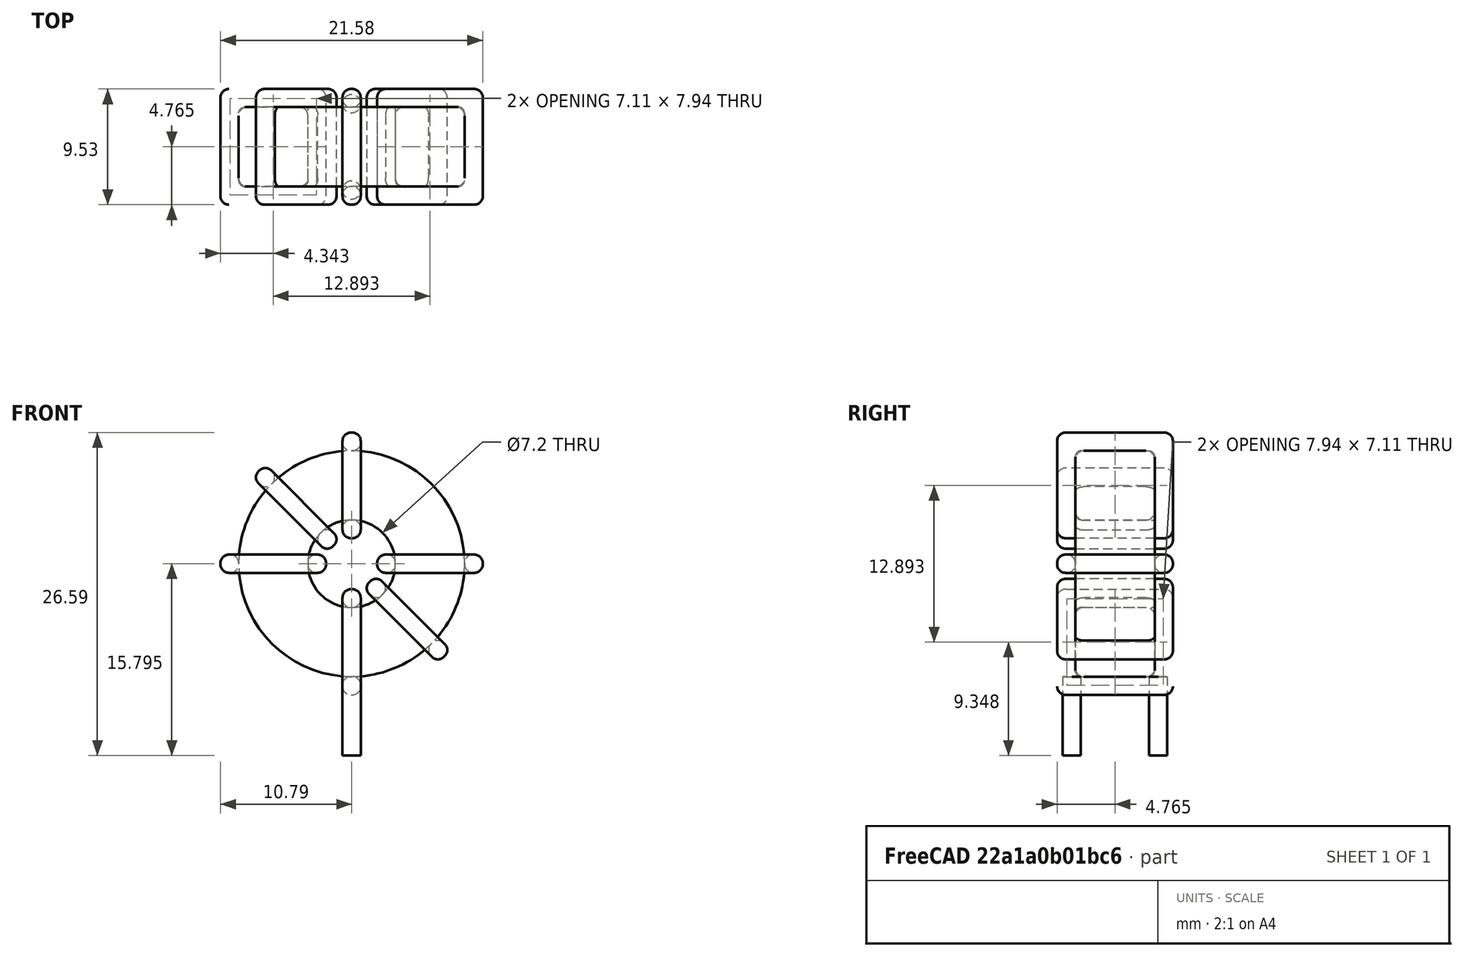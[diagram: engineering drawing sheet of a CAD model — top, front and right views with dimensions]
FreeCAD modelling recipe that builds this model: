
FCSTD DOCUMENT  (FreeCAD 0.16R6703 (Git))
Label: L_Toroid_Vertical_L21.6mm_W9.5mm_P7.11mm_Pulse_C
License: All rights reserved
LicenseURL: http://en.wikipedia.org/wiki/All_rights_reserved
objects: Sketcher::SketchObject×6, PartDesign::Pad×6, PartDesign::Fillet×5, Spreadsheet::Sheet×1
note: 23 computed .brp shape members not serialized (recipe doc carries the construction recipe); baked Part::Feature solids carry a one-line shape summary decoded from their .brp

FEATURE [Spreadsheet::Sheet] Spreadsheet  label="dimensions"
  cells = A1=Wx; B1(Wx)=21.59; C1(WW)=7.196666666666666; D1=21.59; A2=Wy; B2(Wy)=9.529999999999999; D2=9.529999999999999; A3=RM; B3(RMx)=7.11; C3(RMy)=0; A4=d_wire; B4(d_wire)=1.5; A5=H; B5(H)=21.59; A6=offsetx; B6(offsetx)=10.795
FEATURE [Sketcher::SketchObject] Sketch
  Placement = pos=(0,-3.555,0) rot=(1,0,0;1.5708rad)
  expr: Placement.Base.y = -Spreadsheet.RMx / 2
  expr: Constraints[0] = Spreadsheet.Wx / 2 - Spreadsheet.d_wire
  expr: Constraints[4] = Spreadsheet.WW / 2
  expr: Constraints[2] = Spreadsheet.Wx / 2 + Spreadsheet.d_wire + 0.5
  sketch-geometry (2):
    g0: Circle CenterX=0 CenterY=12.795 CenterZ=0 NormalX=0 NormalY=0 NormalZ=1 Radius=9.295
    g1: Circle CenterX=0 CenterY=12.795 CenterZ=0 NormalX=0 NormalY=0 NormalZ=1 Radius=3.59833
  constraints (5):
    c: Radius(g0) = 9.295
    c: DistanceX(g-1,g0) = 0
    c: DistanceY(g-1,g0) = 12.795
    c: Coincident(g1,g0)
    c: Radius(g1) = 3.59833
FEATURE [PartDesign::Pad] Pad
  Length = 6.53
  Length2 = 100
  Midplane = true
  Placement = pos=(0,-3.555,0) rot=(1,0,0;1.5708rad)
  Sketch = -> Sketch
  Type = 0
  expr: Length = Spreadsheet.Wy - 2 * Spreadsheet.d_wire
FEATURE [Sketcher::SketchObject] Sketch001
  Placement = pos=(0,0,2) rot=(0,0,1;0rad)
  expr: Placement.Base.z = 0.5 + Spreadsheet.d_wire
  expr: Constraints[4] = Spreadsheet.RMy
  expr: Constraints[2] = -Spreadsheet.RMx
  expr: Constraints[1] = Spreadsheet.d_wire / 2
  sketch-geometry (2):
    g0: Circle CenterX=0 CenterY=0 CenterZ=0 NormalX=0 NormalY=0 NormalZ=1 Radius=0.75
    g1: Circle CenterX=0 CenterY=-7.11 CenterZ=0 NormalX=0 NormalY=0 NormalZ=1 Radius=0.75
  constraints (5):
    c: Equal(g0,g1)
    c: Radius(g0) = 0.75
    c: DistanceY(g-1,g1) = -7.11
    c: Coincident(g0,g-1)
    c: DistanceX(g-1,g1) = 0
FEATURE [PartDesign::Pad] Pad001
  Length = 1.5
  Length2 = 5
  Placement = pos=(0,0,2) rot=(0,0,1;0rad)
  Reversed = true
  Sketch = -> Sketch001
  Type = 4
  expr: Length2 = 3.5 + Spreadsheet.d_wire
  expr: Length = Spreadsheet.d_wire
FEATURE [PartDesign::Fillet] Fillet
  Base = -> Pad [Edge6,Edge3,Edge2]
  Placement = pos=(0,-3.555,0) rot=(1,0,0;1.5708rad)
  Radius = 0.5
FEATURE [Sketcher::SketchObject] Sketch003
  Placement = pos=(0,1.21,12.795) rot=(1,0,0;3.14159rad)
  expr: Constraints[18] = Spreadsheet.d_wire
  expr: Constraints[16] = Spreadsheet.d_wire
  expr: Constraints[19] = Spreadsheet.d_wire
  expr: Constraints[17] = Spreadsheet.d_wire
  expr: Placement.Base.y = -1 * (Spreadsheet.RMx - Spreadsheet.Wy) / 2
  expr: Constraints[21] = (Spreadsheet.Wx - Spreadsheet.WW) / 2 - Spreadsheet.d_wire
  expr: Constraints[22] = Spreadsheet.Wx / 2 - Spreadsheet.d_wire
  expr: Constraints[43] = Spreadsheet.d_wire
  expr: Constraints[48] = Spreadsheet.Wx - Spreadsheet.d_wire * 2
  expr: Constraints[49] = Spreadsheet.Wy
  expr: Placement.Base.z = Spreadsheet.Wx / 2 + Spreadsheet.d_wire + 0.5
  sketch-geometry (16):
    g0: LineSegment StartX=-2.09833 StartY=0 StartZ=0 EndX=-10.795 EndY=0 EndZ=0
    g1: LineSegment StartX=-10.795 StartY=0 StartZ=0 EndX=-10.795 EndY=9.53 EndZ=0
    g2: LineSegment StartX=-10.795 StartY=9.53 StartZ=0 EndX=-2.09833 EndY=9.53 EndZ=0
    g3: LineSegment StartX=-2.09833 StartY=9.53 StartZ=0 EndX=-2.09833 EndY=0 EndZ=0
    g4: LineSegment StartX=-9.295 StartY=8.03 StartZ=0 EndX=-3.59833 EndY=8.03 EndZ=0
    g5: LineSegment StartX=-3.59833 StartY=8.03 StartZ=0 EndX=-3.59833 EndY=1.5 EndZ=0
    g6: LineSegment StartX=-3.59833 StartY=1.5 StartZ=0 EndX=-9.295 EndY=1.5 EndZ=0
    g7: LineSegment StartX=-9.295 StartY=1.5 StartZ=0 EndX=-9.295 EndY=8.03 EndZ=0
    g8: LineSegment StartX=2.09833 StartY=9.53 StartZ=0 EndX=10.795 EndY=9.53 EndZ=0
    g9: LineSegment StartX=10.795 StartY=9.53 StartZ=0 EndX=10.795 EndY=0 EndZ=0
    g10: LineSegment StartX=10.795 StartY=0 StartZ=0 EndX=2.09833 EndY=0 EndZ=0
    g11: LineSegment StartX=2.09833 StartY=0 StartZ=0 EndX=2.09833 EndY=9.53 EndZ=0
    g12: LineSegment StartX=3.59833 StartY=8.03 StartZ=0 EndX=9.295 EndY=8.03 EndZ=0
    g13: LineSegment StartX=9.295 StartY=8.03 StartZ=0 EndX=9.295 EndY=1.5 EndZ=0
    g14: LineSegment StartX=9.295 StartY=1.5 StartZ=0 EndX=3.59833 EndY=1.5 EndZ=0
    g15: LineSegment StartX=3.59833 StartY=1.5 StartZ=0 EndX=3.59833 EndY=8.03 EndZ=0
  constraints (50):
    c: Horizontal(g0)
    c: Coincident(g1,g0)
    c: Vertical(g1)
    c: Coincident(g2,g1)
    c: Horizontal(g2)
    c: Coincident(g3,g2)
    c: Coincident(g3,g0)
    c: Vertical(g3)
    c: Coincident(g4,g5)
    c: Coincident(g5,g6)
    c: Coincident(g6,g7)
    c: Coincident(g7,g4)
    c: Horizontal(g4)
    c: Horizontal(g6)
    c: Vertical(g5)
    c: Vertical(g7)
    c: DistanceX(g1,g4) = 1.5
    c: DistanceY(g4,g1) = 1.5
    c: DistanceX(g5,g0) = 1.5
    c: DistanceY(g0,g5) = 1.5
    c: DistanceY(g-1,g0) = 0
    c: DistanceX(g6,g6) = 5.69667
    c: DistanceX(g6,g-1) = 9.295
    c: Coincident(g8,g9)
    c: Coincident(g9,g10)
    c: Coincident(g10,g11)
    c: Coincident(g11,g8)
    c: Horizontal(g8)
    c: Horizontal(g10)
    c: Vertical(g9)
    c: Vertical(g11)
    c: Coincident(g12,g13)
    c: Coincident(g13,g14)
    c: Coincident(g14,g15)
    c: Coincident(g15,g12)
    c: Horizontal(g12)
    c: Horizontal(g14)
    c: Vertical(g13)
    c: Vertical(g15)
    c: DistanceY(g8,g2) = 0
    c: DistanceY(g10,g0) = 0
    c: DistanceY(g14,g5) = 0
    c: DistanceY(g12,g4) = 0
    c: DistanceX(g8,g12) = 1.5
    c: Equal(g8,g2)
    c: Equal(g12,g4)
    c: Equal(g9,g1)
    c: Equal(g13,g7)
    c: DistanceX(g4,g12) = 18.59
    c: DistanceY(g0,g1) = 9.53
FEATURE [PartDesign::Pad] Pad002
  Length = 1.5
  Length2 = 100
  Midplane = true
  Placement = pos=(0,1.21,12.795) rot=(1,0,0;3.14159rad)
  Sketch = -> Sketch003
  Type = 0
  expr: Length = Spreadsheet.d_wire
FEATURE [PartDesign::Fillet] Fillet001
  Base = -> Pad002 [Edge38,Edge41,Edge42,Edge43,Edge29,Edge32,Edge33,Edge34,Edge25,Edge35,Edge36,Edge13,Edge14,Edge15,Edge16,Edge17,Edge18,Edge19,Edge1,Edge2,Edge3,Edge4,Edge5,Edge6,Edge7,Edge37,Edge39,Edge40,Edge20,Edge23,Edge24,Edge21,Edge22,Edge8,Edge9,Edge10,Edge11,Edge12,Edge26,Edge27,+8 more]
  Placement = pos=(0,1.21,12.795) rot=(1,0,0;3.14159rad)
  Radius = 0.705
  expr: Radius = Spreadsheet.d_wire * 0.47
FEATURE [Sketcher::SketchObject] Sketch004
  Placement = pos=(0,1.21,12.795) rot=(0.92388,0,0.382683;3.14159rad)
  expr: Constraints[18] = Spreadsheet.d_wire
  expr: Constraints[16] = Spreadsheet.d_wire
  expr: Constraints[19] = Spreadsheet.d_wire
  expr: Constraints[17] = Spreadsheet.d_wire
  expr: Placement.Base.y = -1 * (Spreadsheet.RMx - Spreadsheet.Wy) / 2
  expr: Constraints[21] = (Spreadsheet.Wx - Spreadsheet.WW) / 2 - Spreadsheet.d_wire
  expr: Constraints[22] = Spreadsheet.Wx / 2 - Spreadsheet.d_wire
  expr: Constraints[43] = Spreadsheet.d_wire
  expr: Constraints[48] = Spreadsheet.Wx - 2 * Spreadsheet.d_wire
  expr: Constraints[49] = Spreadsheet.Wy
  expr: Placement.Base.z = Spreadsheet.Wx / 2 + Spreadsheet.d_wire + 0.5
  sketch-geometry (16):
    g0: LineSegment StartX=-2.09833 StartY=0 StartZ=0 EndX=-10.795 EndY=0 EndZ=0
    g1: LineSegment StartX=-10.795 StartY=0 StartZ=0 EndX=-10.795 EndY=9.53 EndZ=0
    g2: LineSegment StartX=-10.795 StartY=9.53 StartZ=0 EndX=-2.09833 EndY=9.53 EndZ=0
    g3: LineSegment StartX=-2.09833 StartY=9.53 StartZ=0 EndX=-2.09833 EndY=0 EndZ=0
    g4: LineSegment StartX=-9.295 StartY=8.03 StartZ=0 EndX=-3.59833 EndY=8.03 EndZ=0
    g5: LineSegment StartX=-3.59833 StartY=8.03 StartZ=0 EndX=-3.59833 EndY=1.5 EndZ=0
    g6: LineSegment StartX=-3.59833 StartY=1.5 StartZ=0 EndX=-9.295 EndY=1.5 EndZ=0
    g7: LineSegment StartX=-9.295 StartY=1.5 StartZ=0 EndX=-9.295 EndY=8.03 EndZ=0
    g8: LineSegment StartX=2.09833 StartY=9.53 StartZ=0 EndX=10.795 EndY=9.53 EndZ=0
    g9: LineSegment StartX=10.795 StartY=9.53 StartZ=0 EndX=10.795 EndY=0 EndZ=0
    g10: LineSegment StartX=10.795 StartY=0 StartZ=0 EndX=2.09833 EndY=0 EndZ=0
    g11: LineSegment StartX=2.09833 StartY=0 StartZ=0 EndX=2.09833 EndY=9.53 EndZ=0
    g12: LineSegment StartX=3.59833 StartY=8.03 StartZ=0 EndX=9.295 EndY=8.03 EndZ=0
    g13: LineSegment StartX=9.295 StartY=8.03 StartZ=0 EndX=9.295 EndY=1.5 EndZ=0
    g14: LineSegment StartX=9.295 StartY=1.5 StartZ=0 EndX=3.59833 EndY=1.5 EndZ=0
    g15: LineSegment StartX=3.59833 StartY=1.5 StartZ=0 EndX=3.59833 EndY=8.03 EndZ=0
  constraints (50):
    c: Horizontal(g0)
    c: Coincident(g1,g0)
    c: Vertical(g1)
    c: Coincident(g2,g1)
    c: Horizontal(g2)
    c: Coincident(g3,g2)
    c: Coincident(g3,g0)
    c: Vertical(g3)
    c: Coincident(g4,g5)
    c: Coincident(g5,g6)
    c: Coincident(g6,g7)
    c: Coincident(g7,g4)
    c: Horizontal(g4)
    c: Horizontal(g6)
    c: Vertical(g5)
    c: Vertical(g7)
    c: DistanceX(g1,g4) = 1.5
    c: DistanceY(g4,g1) = 1.5
    c: DistanceX(g5,g0) = 1.5
    c: DistanceY(g0,g5) = 1.5
    c: DistanceY(g-1,g0) = 0
    c: DistanceX(g6,g6) = 5.69667
    c: DistanceX(g6,g-1) = 9.295
    c: Coincident(g8,g9)
    c: Coincident(g9,g10)
    c: Coincident(g10,g11)
    c: Coincident(g11,g8)
    c: Horizontal(g8)
    c: Horizontal(g10)
    c: Vertical(g9)
    c: Vertical(g11)
    c: Coincident(g12,g13)
    c: Coincident(g13,g14)
    c: Coincident(g14,g15)
    c: Coincident(g15,g12)
    c: Horizontal(g12)
    c: Horizontal(g14)
    c: Vertical(g13)
    c: Vertical(g15)
    c: DistanceY(g8,g2) = 0
    c: DistanceY(g10,g0) = 0
    c: DistanceY(g14,g5) = 0
    c: DistanceY(g12,g4) = 0
    c: DistanceX(g8,g12) = 1.5
    c: Equal(g8,g2)
    c: Equal(g12,g4)
    c: Equal(g9,g1)
    c: Equal(g13,g7)
    c: DistanceX(g4,g12) = 18.59
    c: DistanceY(g0,g1) = 9.53
FEATURE [PartDesign::Pad] Pad003
  Length = 1.5
  Length2 = 100
  Midplane = true
  Placement = pos=(0,1.21,12.795) rot=(0.92388,0,0.382683;3.14159rad)
  Sketch = -> Sketch004
  Type = 0
  expr: Length = Spreadsheet.d_wire
FEATURE [PartDesign::Fillet] Fillet002
  Base = -> Pad003 [Edge38,Edge41,Edge42,Edge43,Edge29,Edge32,Edge33,Edge34,Edge25,Edge35,Edge36,Edge13,Edge14,Edge15,Edge16,Edge17,Edge18,Edge19,Edge1,Edge2,Edge3,Edge4,Edge5,Edge6,Edge7,Edge37,Edge39,Edge40,Edge20,Edge23,Edge24,Edge21,Edge22,Edge8,Edge9,Edge10,Edge11,Edge12,Edge26,Edge27,+8 more]
  Placement = pos=(0,1.21,12.795) rot=(0.92388,0,0.382683;3.14159rad)
  Radius = 0.705
  expr: Radius = Spreadsheet.d_wire * 0.47
FEATURE [Sketcher::SketchObject] Sketch005
  Placement = pos=(0,1.21,12.795) rot=(0.92388,0,-0.382683;3.14159rad)
  expr: Constraints[18] = Spreadsheet.d_wire
  expr: Constraints[16] = Spreadsheet.d_wire
  expr: Constraints[19] = Spreadsheet.d_wire
  expr: Constraints[17] = Spreadsheet.d_wire
  expr: Placement.Base.y = -1 * (Spreadsheet.RMx - Spreadsheet.Wy) / 2
  expr: Constraints[21] = (Spreadsheet.Wx - Spreadsheet.WW) / 2 - Spreadsheet.d_wire
  expr: Constraints[22] = Spreadsheet.Wx / 2 - Spreadsheet.d_wire
  expr: Constraints[43] = Spreadsheet.d_wire
  expr: Constraints[48] = Spreadsheet.Wx - 2 * Spreadsheet.d_wire
  expr: Constraints[49] = Spreadsheet.Wy
  expr: Placement.Base.z = Spreadsheet.Wx / 2 + Spreadsheet.d_wire + 0.5
  sketch-geometry (16):
    g0: LineSegment StartX=-2.09833 StartY=0 StartZ=0 EndX=-10.795 EndY=0 EndZ=0
    g1: LineSegment StartX=-10.795 StartY=0 StartZ=0 EndX=-10.795 EndY=9.53 EndZ=0
    g2: LineSegment StartX=-10.795 StartY=9.53 StartZ=0 EndX=-2.09833 EndY=9.53 EndZ=0
    g3: LineSegment StartX=-2.09833 StartY=9.53 StartZ=0 EndX=-2.09833 EndY=0 EndZ=0
    g4: LineSegment StartX=-9.295 StartY=8.03 StartZ=0 EndX=-3.59833 EndY=8.03 EndZ=0
    g5: LineSegment StartX=-3.59833 StartY=8.03 StartZ=0 EndX=-3.59833 EndY=1.5 EndZ=0
    g6: LineSegment StartX=-3.59833 StartY=1.5 StartZ=0 EndX=-9.295 EndY=1.5 EndZ=0
    g7: LineSegment StartX=-9.295 StartY=1.5 StartZ=0 EndX=-9.295 EndY=8.03 EndZ=0
    g8: LineSegment StartX=2.09833 StartY=9.53 StartZ=0 EndX=10.795 EndY=9.53 EndZ=0
    g9: LineSegment StartX=10.795 StartY=9.53 StartZ=0 EndX=10.795 EndY=0 EndZ=0
    g10: LineSegment StartX=10.795 StartY=0 StartZ=0 EndX=2.09833 EndY=0 EndZ=0
    g11: LineSegment StartX=2.09833 StartY=0 StartZ=0 EndX=2.09833 EndY=9.53 EndZ=0
    g12: LineSegment StartX=3.59833 StartY=8.03 StartZ=0 EndX=9.295 EndY=8.03 EndZ=0
    g13: LineSegment StartX=9.295 StartY=8.03 StartZ=0 EndX=9.295 EndY=1.5 EndZ=0
    g14: LineSegment StartX=9.295 StartY=1.5 StartZ=0 EndX=3.59833 EndY=1.5 EndZ=0
    g15: LineSegment StartX=3.59833 StartY=1.5 StartZ=0 EndX=3.59833 EndY=8.03 EndZ=0
  constraints (50):
    c: Horizontal(g0)
    c: Coincident(g1,g0)
    c: Vertical(g1)
    c: Coincident(g2,g1)
    c: Horizontal(g2)
    c: Coincident(g3,g2)
    c: Coincident(g3,g0)
    c: Vertical(g3)
    c: Coincident(g4,g5)
    c: Coincident(g5,g6)
    c: Coincident(g6,g7)
    c: Coincident(g7,g4)
    c: Horizontal(g4)
    c: Horizontal(g6)
    c: Vertical(g5)
    c: Vertical(g7)
    c: DistanceX(g1,g4) = 1.5
    c: DistanceY(g4,g1) = 1.5
    c: DistanceX(g5,g0) = 1.5
    c: DistanceY(g0,g5) = 1.5
    c: DistanceY(g-1,g0) = 0
    c: DistanceX(g6,g6) = 5.69667
    c: DistanceX(g6,g-1) = 9.295
    c: Coincident(g8,g9)
    c: Coincident(g9,g10)
    c: Coincident(g10,g11)
    c: Coincident(g11,g8)
    c: Horizontal(g8)
    c: Horizontal(g10)
    c: Vertical(g9)
    c: Vertical(g11)
    c: Coincident(g12,g13)
    c: Coincident(g13,g14)
    c: Coincident(g14,g15)
    c: Coincident(g15,g12)
    c: Horizontal(g12)
    c: Horizontal(g14)
    c: Vertical(g13)
    c: Vertical(g15)
    c: DistanceY(g8,g2) = 0
    c: DistanceY(g10,g0) = 0
    c: DistanceY(g14,g5) = 0
    c: DistanceY(g12,g4) = 0
    c: DistanceX(g8,g12) = 1.5
    c: Equal(g8,g2)
    c: Equal(g12,g4)
    c: Equal(g9,g1)
    c: Equal(g13,g7)
    c: DistanceX(g4,g12) = 18.59
    c: DistanceY(g0,g1) = 9.53
FEATURE [PartDesign::Pad] Pad004
  Length = 1.5
  Length2 = 100
  Midplane = true
  Placement = pos=(0,1.21,12.795) rot=(0.92388,0,-0.382683;3.14159rad)
  Sketch = -> Sketch005
  Type = 0
  expr: Length = Spreadsheet.d_wire
FEATURE [PartDesign::Fillet] Fillet003
  Base = -> Pad004 [Edge38,Edge41,Edge42,Edge43,Edge29,Edge32,Edge33,Edge34,Edge25,Edge35,Edge36,Edge13,Edge14,Edge15,Edge16,Edge17,Edge18,Edge19,Edge1,Edge2,Edge3,Edge4,Edge5,Edge6,Edge7,Edge37,Edge39,Edge40,Edge20,Edge23,Edge24,Edge21,Edge22,Edge8,Edge9,Edge10,Edge11,Edge12,Edge26,Edge27,+8 more]
  Placement = pos=(0,1.21,12.795) rot=(0.92388,0,-0.382683;3.14159rad)
  Radius = 0.705
  expr: Radius = Spreadsheet.d_wire * 0.47
FEATURE [Sketcher::SketchObject] Sketch006
  Placement = pos=(0,1.21,12.795) rot=(0.707107,0,0.707107;3.14159rad)
  expr: Constraints[18] = Spreadsheet.d_wire
  expr: Constraints[16] = Spreadsheet.d_wire
  expr: Constraints[19] = Spreadsheet.d_wire
  expr: Constraints[17] = Spreadsheet.d_wire
  expr: Placement.Base.y = -1 * (Spreadsheet.RMx - Spreadsheet.Wy) / 2
  expr: Constraints[21] = (Spreadsheet.Wx - Spreadsheet.WW) / 2 - Spreadsheet.d_wire
  expr: Constraints[22] = Spreadsheet.Wx / 2 - Spreadsheet.d_wire
  expr: Constraints[43] = Spreadsheet.d_wire
  expr: Constraints[48] = Spreadsheet.Wx - Spreadsheet.d_wire * 2
  expr: Constraints[49] = Spreadsheet.Wy
  expr: Placement.Base.z = Spreadsheet.Wx / 2 + Spreadsheet.d_wire + 0.5
  sketch-geometry (16):
    g0: LineSegment StartX=-2.09833 StartY=0 StartZ=0 EndX=-10.795 EndY=0 EndZ=0
    g1: LineSegment StartX=-10.795 StartY=0 StartZ=0 EndX=-10.795 EndY=9.53 EndZ=0
    g2: LineSegment StartX=-10.795 StartY=9.53 StartZ=0 EndX=-2.09833 EndY=9.53 EndZ=0
    g3: LineSegment StartX=-2.09833 StartY=9.53 StartZ=0 EndX=-2.09833 EndY=0 EndZ=0
    g4: LineSegment StartX=-9.295 StartY=8.03 StartZ=0 EndX=-3.59833 EndY=8.03 EndZ=0
    g5: LineSegment StartX=-3.59833 StartY=8.03 StartZ=0 EndX=-3.59833 EndY=1.5 EndZ=0
    g6: LineSegment StartX=-3.59833 StartY=1.5 StartZ=0 EndX=-9.295 EndY=1.5 EndZ=0
    g7: LineSegment StartX=-9.295 StartY=1.5 StartZ=0 EndX=-9.295 EndY=8.03 EndZ=0
    g8: LineSegment StartX=2.09833 StartY=9.53 StartZ=0 EndX=10.795 EndY=9.53 EndZ=0
    g9: LineSegment StartX=10.795 StartY=9.53 StartZ=0 EndX=10.795 EndY=0 EndZ=0
    g10: LineSegment StartX=10.795 StartY=0 StartZ=0 EndX=2.09833 EndY=0 EndZ=0
    g11: LineSegment StartX=2.09833 StartY=0 StartZ=0 EndX=2.09833 EndY=9.53 EndZ=0
    g12: LineSegment StartX=3.59833 StartY=8.03 StartZ=0 EndX=9.295 EndY=8.03 EndZ=0
    g13: LineSegment StartX=9.295 StartY=8.03 StartZ=0 EndX=9.295 EndY=1.5 EndZ=0
    g14: LineSegment StartX=9.295 StartY=1.5 StartZ=0 EndX=3.59833 EndY=1.5 EndZ=0
    g15: LineSegment StartX=3.59833 StartY=1.5 StartZ=0 EndX=3.59833 EndY=8.03 EndZ=0
  constraints (50):
    c: Horizontal(g0)
    c: Coincident(g1,g0)
    c: Vertical(g1)
    c: Coincident(g2,g1)
    c: Horizontal(g2)
    c: Coincident(g3,g2)
    c: Coincident(g3,g0)
    c: Vertical(g3)
    c: Coincident(g4,g5)
    c: Coincident(g5,g6)
    c: Coincident(g6,g7)
    c: Coincident(g7,g4)
    c: Horizontal(g4)
    c: Horizontal(g6)
    c: Vertical(g5)
    c: Vertical(g7)
    c: DistanceX(g1,g4) = 1.5
    c: DistanceY(g4,g1) = 1.5
    c: DistanceX(g5,g0) = 1.5
    c: DistanceY(g0,g5) = 1.5
    c: DistanceY(g-1,g0) = 0
    c: DistanceX(g6,g6) = 5.69667
    c: DistanceX(g6,g-1) = 9.295
    c: Coincident(g8,g9)
    c: Coincident(g9,g10)
    c: Coincident(g10,g11)
    c: Coincident(g11,g8)
    c: Horizontal(g8)
    c: Horizontal(g10)
    c: Vertical(g9)
    c: Vertical(g11)
    c: Coincident(g12,g13)
    c: Coincident(g13,g14)
    c: Coincident(g14,g15)
    c: Coincident(g15,g12)
    c: Horizontal(g12)
    c: Horizontal(g14)
    c: Vertical(g13)
    c: Vertical(g15)
    c: DistanceY(g8,g2) = 0
    c: DistanceY(g10,g0) = 0
    c: DistanceY(g14,g5) = 0
    c: DistanceY(g12,g4) = 0
    c: DistanceX(g8,g12) = 1.5
    c: Equal(g8,g2)
    c: Equal(g12,g4)
    c: Equal(g9,g1)
    c: Equal(g13,g7)
    c: DistanceX(g4,g12) = 18.59
    c: DistanceY(g0,g1) = 9.53
FEATURE [PartDesign::Pad] Pad005
  Length = 1.5
  Length2 = 100
  Midplane = true
  Placement = pos=(0,1.21,12.795) rot=(0.707107,0,0.707107;3.14159rad)
  Sketch = -> Sketch006
  Type = 0
  expr: Length = Spreadsheet.d_wire
FEATURE [PartDesign::Fillet] Fillet004
  Base = -> Pad005 [Edge38,Edge41,Edge42,Edge43,Edge29,Edge32,Edge33,Edge34,Edge25,Edge35,Edge36,Edge13,Edge14,Edge15,Edge16,Edge17,Edge18,Edge19,Edge1,Edge2,Edge3,Edge4,Edge5,Edge6,Edge7,Edge37,Edge39,Edge40,Edge20,Edge23,Edge24,Edge21,Edge22,Edge8,Edge9,Edge10,Edge11,Edge12,Edge26,Edge27,+8 more]
  Placement = pos=(0,1.21,12.795) rot=(0.707107,0,0.707107;3.14159rad)
  Radius = 0.705
  expr: Radius = Spreadsheet.d_wire * 0.47
